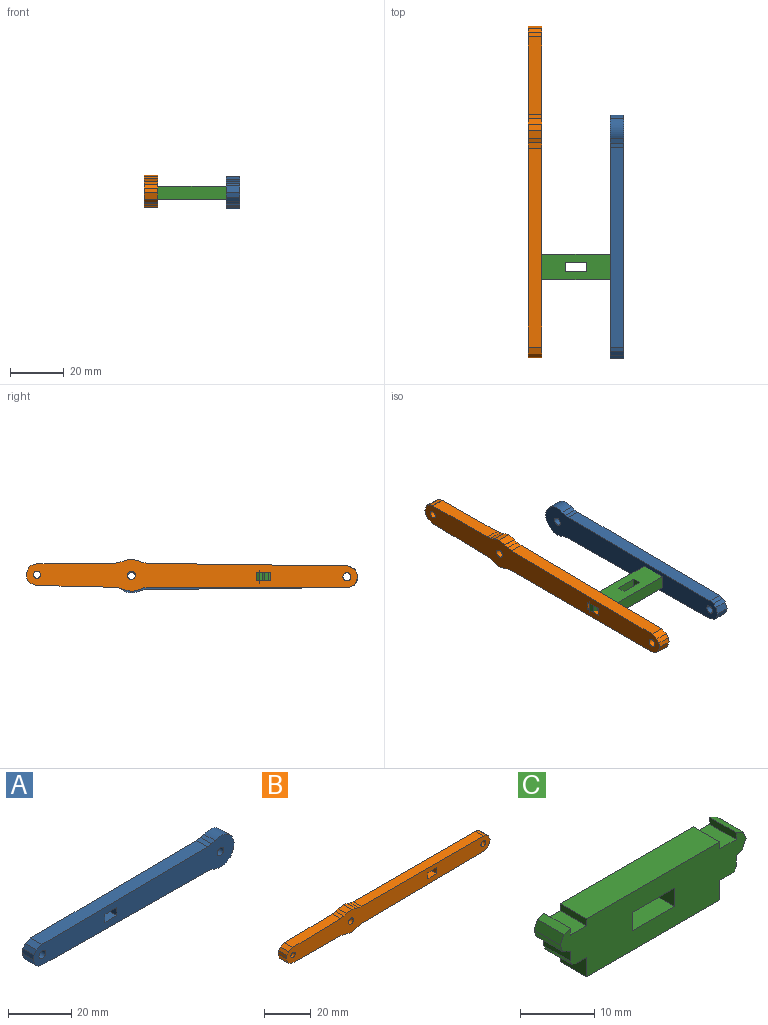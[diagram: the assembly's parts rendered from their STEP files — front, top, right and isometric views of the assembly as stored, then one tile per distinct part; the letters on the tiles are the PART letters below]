
ASSEMBLY  parts=3 mates=2
PART A: 23 faces, bbox 90.1x5x12 mm
  f0: plane 5x1.84mm, normal (-0.3,0,-0.95), area 9.7mm2, adj f1,f17,f20,f21
  f1: cylinder r=6mm len=7.21mm, axis (0,1,0), area 40mm2, adj f0,f2,f20,f21
  f2: cylinder r=6mm len=7.42mm, axis (0,1,0), area 40mm2, adj f1,f3,f20,f21
  f3: cylinder r=6mm len=7.21mm, axis (0,1,0), area 40mm2, adj f2,f4,f20,f21
  f4: plane 5x1.43mm, normal (-0.32,0,0.95), area 7.6mm2, adj f3,f5,f20,f21
  f5: plane 5x1.92mm, normal (-0.12,0,0.99), area 9.7mm2, adj f4,f6,f20,f21
  f6: plane 74.29x5mm, normal (-0.01,0,1), area 371.5mm2, adj f5,f7,f20,f21
  f7: plane 5x2.53mm, normal (-0.35,0,0.94), area 13.5mm2, adj f6,f8,f20,f21
  f8: plane 5x1.35mm, normal (-0.79,0,0.61), area 8.5mm2, adj f7,f9,f20,f21
  f9: plane 5x1.72mm, normal (-0.98,0,0.22), area 8.8mm2, adj f8,f10,f20,f21
  f10: plane 5x2.54mm, normal (-0.94,0,-0.34), area 13.5mm2, adj f9,f11,f20,f21
  f11: plane 5x1.34mm, normal (-0.62,0,-0.78), area 8.5mm2, adj f10,f12,f20,f21
  f12: plane 5x1.71mm, normal (-0.23,0,-0.97), area 8.8mm2, adj f11,f13,f20,f21
  f13: plane 74.29x5mm, normal (-0.01,0,-1), area 371.5mm2, adj f12,f17,f20,f21
  f14: plane 5x3.1mm, normal (1,0,0), area 15.5mm2, adj f15,f18,f20,f21
  f15: plane 5.37x5mm, normal (0,0,-1), area 26.9mm2, adj f14,f16,f20,f21
  f16: plane 5x3.1mm, normal (-1,0,0), area 15.5mm2, adj f15,f18,f20,f21
  f17: plane 5x1.51mm, normal (-0.1,0,-1), area 7.6mm2, adj f0,f13,f20,f21
  f18: plane 5.37x5mm, normal (0,0,1), area 26.9mm2, adj f14,f16,f20,f21
  f19: cylinder r=1.5mm len=5mm, axis (0,1,0), area 47.1mm2, adj f20,f21
  f20: plane 90.1x12mm, normal (0,-1,0), area 760.4mm2, adj f0,f1,f2,f3,f4,f5,f6,f7
  f21: plane 90.1x12mm, normal (0,1,0), area 760.4mm2, adj f0,f1,f2,f3,f4,f5,f6,f7
  f22: cylinder r=1.5mm len=5mm, axis (0,-1,0), area 47.1mm2, adj f20,f21
PART B: 41 faces, bbox 123.1x5x12 mm
  f0: plane 5x3.1mm, normal (-1,0,0), area 15.5mm2, adj f1,f35,f39,f40
  f1: plane 5.37x5mm, normal (0,0,1), area 26.9mm2, adj f0,f2,f39,f40
  f2: plane 5x3.1mm, normal (1,0,0), area 15.5mm2, adj f1,f35,f39,f40
  f3: plane 5x1.71mm, normal (-0.23,0,-0.97), area 8.8mm2, adj f4,f36,f39,f40
  f4: plane 5x0.1mm, normal (0,0,-1), area 0.5mm2, adj f3,f5,f39,f40
  f5: plane 28.82x5mm, normal (-0.01,0,-1), area 144.1mm2, adj f4,f6,f39,f40
  f6: plane 5x1.6mm, normal (-0.11,0,-0.99), area 8mm2, adj f5,f7,f39,f40
  f7: plane 5x1.93mm, normal (-0.33,0,-0.94), area 10.2mm2, adj f6,f8,f39,f40
  f8: plane 5x0.06mm, normal (-0.16,0,-0.99), area 0.3mm2, adj f7,f9,f39,f40
  f9: plane 5x2.39mm, normal (-0.27,0,-0.96), area 12.4mm2, adj f8,f10,f39,f40
  f10: plane 5x3.06mm, normal (0.2,0,-0.98), area 15.6mm2, adj f9,f11,f39,f40
  f11: plane 5x0.06mm, normal (0.74,0,0.67), area 0.4mm2, adj f10,f12,f39,f40
  f12: plane 5x1.51mm, normal (0.37,0,-0.93), area 8.1mm2, adj f11,f13,f39,f40
  f13: plane 5x2.05mm, normal (0.14,0,-0.99), area 10.3mm2, adj f12,f14,f39,f40
  f14: plane 73.74x5mm, normal (0.01,0,-1), area 368.7mm2, adj f13,f15,f39,f40
  f15: plane 5x2.54mm, normal (0.35,0,-0.94), area 13.5mm2, adj f14,f16,f39,f40
  f16: plane 5x1.35mm, normal (0.79,0,-0.61), area 8.5mm2, adj f15,f17,f39,f40
  f17: plane 5x1.72mm, normal (0.98,0,-0.21), area 8.8mm2, adj f16,f18,f39,f40
  f18: plane 5x2.54mm, normal (0.94,0,0.34), area 13.5mm2, adj f17,f19,f39,f40
  f19: plane 5x1.35mm, normal (0.61,0,0.79), area 8.5mm2, adj f18,f20,f39,f40
  f20: plane 5x1.72mm, normal (0.22,0,0.98), area 8.8mm2, adj f19,f21,f39,f40
  f21: plane 73.75x5mm, normal (0,0,1), area 368.7mm2, adj f20,f22,f39,f40
  f22: plane 5x1.62mm, normal (0.1,0,0.99), area 8.1mm2, adj f21,f23,f39,f40
  f23: plane 5x1.95mm, normal (0.33,0,0.94), area 10.3mm2, adj f22,f24,f39,f40
  f24: plane 5x2.39mm, normal (0.25,0,0.97), area 12.4mm2, adj f23,f25,f39,f40
  f25: plane 5x3.06mm, normal (-0.21,0,0.98), area 15.6mm2, adj f24,f26,f39,f40
  f26: plane 5x1.49mm, normal (-0.37,0,0.93), area 8mm2, adj f25,f27,f39,f40
  f27: plane 5x2.02mm, normal (-0.15,0,0.99), area 10.2mm2, adj f26,f28,f39,f40
  f28: plane 28.81x5mm, normal (-0.02,0,1), area 144.1mm2, adj f27,f29,f39,f40
  f29: plane 5x0.1mm, normal (0,0,1), area 0.5mm2, adj f28,f30,f39,f40
  f30: plane 5x2.51mm, normal (-0.36,0,0.93), area 13.5mm2, adj f29,f31,f39,f40
  f31: plane 5x1.35mm, normal (-0.8,0,0.6), area 8.5mm2, adj f30,f32,f39,f40
  f32: plane 5x1.71mm, normal (-0.98,0,0.21), area 8.8mm2, adj f31,f33,f39,f40
  f33: plane 5x2.53mm, normal (-0.94,0,-0.34), area 13.5mm2, adj f32,f36,f39,f40
  f34: cylinder r=1.5mm len=5mm, axis (0,1,0), area 47.1mm2, adj f39,f40
  f35: plane 5.37x5mm, normal (0,0,-1), area 26.9mm2, adj f0,f2,f39,f40
  f36: plane 5x1.33mm, normal (-0.62,0,-0.79), area 8.5mm2, adj f3,f33,f39,f40
  f37: cylinder r=1.5mm len=5mm, axis (0,1,0), area 47.1mm2, adj f39,f40
  f38: cylinder r=1.32mm len=5mm, axis (0,1,0), area 41.6mm2, adj f39,f40
  f39: plane 123.1x12.02mm, normal (0,-1,0), area 1011mm2, adj f0,f1,f2,f3,f4,f5,f6,f7
  f40: plane 123.1x12.02mm, normal (0,1,0), area 1011mm2, adj f0,f1,f2,f3,f4,f5,f6,f7
PART C: 32 faces, bbox 35.3x5x9.5 mm
  f0: plane 5x3mm, normal (1,0,0), area 15mm2, adj f1,f29,f30,f31
  f1: plane 8x5mm, normal (0,0,-1), area 40mm2, adj f0,f2,f30,f31
  f2: plane 5x3mm, normal (-1,0,0), area 15mm2, adj f1,f29,f30,f31
  f3: plane 5x1.18mm, normal (0.36,0,-0.93), area 6.3mm2, adj f4,f28,f30,f31
  f4: plane 5x1.42mm, normal (0.9,0,-0.44), area 7.9mm2, adj f3,f5,f30,f31
  f5: plane 5x1.25mm, normal (0.93,0,0.38), area 6.7mm2, adj f4,f6,f30,f31
  f6: plane 5x1.37mm, normal (0.42,0,0.91), area 7.5mm2, adj f5,f7,f30,f31
  f7: plane 5x1.12mm, normal (-1,0,0), area 5.6mm2, adj f6,f8,f30,f31
  f8: plane 5x3.1mm, normal (0,0,1), area 15.5mm2, adj f7,f9,f30,f31
  f9: plane 5x1.13mm, normal (1,0,0), area 5.6mm2, adj f8,f10,f30,f31
  f10: plane 25.3x5mm, normal (0,0,1), area 126.5mm2, adj f9,f11,f30,f31
  f11: plane 5x1.13mm, normal (-1,0,0), area 5.6mm2, adj f10,f12,f30,f31
  f12: plane 5x3.1mm, normal (0,0,1), area 15.5mm2, adj f11,f13,f30,f31
  f13: plane 5x1.11mm, normal (1,0,0), area 5.5mm2, adj f12,f14,f30,f31
  f14: plane 5x1.18mm, normal (-0.32,0,0.95), area 6.3mm2, adj f13,f15,f30,f31
  f15: plane 5x1.47mm, normal (-0.9,0,0.43), area 8.1mm2, adj f14,f16,f30,f31
  f16: plane 5x1.24mm, normal (-0.94,0,-0.34), area 6.6mm2, adj f15,f17,f30,f31
  f17: plane 5x1.43mm, normal (-0.41,0,-0.91), area 7.8mm2, adj f16,f18,f30,f31
  f18: plane 5x1.6mm, normal (-1,0,0), area 8mm2, adj f17,f19,f30,f31
  f19: plane 5x0.74mm, normal (-0.92,0,-0.39), area 4mm2, adj f18,f20,f30,f31
  f20: plane 5x0.79mm, normal (-0.29,0,-0.96), area 4.1mm2, adj f19,f21,f30,f31
  f21: plane 5x2mm, normal (0,0,-1), area 10mm2, adj f20,f22,f30,f31
  f22: plane 5x3.21mm, normal (-1,0,0), area 16mm2, adj f21,f23,f30,f31
  f23: plane 25.3x5mm, normal (0,0,-1), area 126.5mm2, adj f22,f24,f30,f31
  f24: plane 5x3.21mm, normal (1,0,0), area 16mm2, adj f23,f25,f30,f31
  f25: plane 5x2.31mm, normal (0,0,-1), area 11.5mm2, adj f24,f26,f30,f31
  f26: plane 5x0.49mm, normal (0.29,0,-0.96), area 2.5mm2, adj f25,f27,f30,f31
  f27: plane 5x0.63mm, normal (0.9,0,-0.44), area 3.5mm2, adj f26,f28,f30,f31
  f28: plane 5x1.8mm, normal (1,0,0), area 9mm2, adj f3,f27,f30,f31
  f29: plane 8x5mm, normal (0,0,1), area 40mm2, adj f0,f2,f30,f31
  f30: plane 35.25x9.54mm, normal (0,-1,0), area 259mm2, adj f0,f1,f2,f3,f4,f5,f6,f7
  f31: plane 35.25x9.54mm, normal (0,1,0), area 259mm2, adj f0,f1,f2,f3,f4,f5,f6,f7
PLACE A rot(axis=(-0.71,-0.71,0),180deg) t=(17.65,60.52,79.43)mm
PLACE B rot(axis=(-0.71,0.71,0),180deg) t=(-17.65,-36.83,91.13)mm
PLACE C rot(axis=(-1,0,0),90deg) t=(19.63,-42.58,0)mm
MATE fastened A.f22 <-> B.f34  axis (-1,0,0) through (12.65,-29.91,2.5)mm
MATE fastened A.f20 <-> C.f24  axis (-1,0,0) through (12.65,-1.81,2.5)mm
